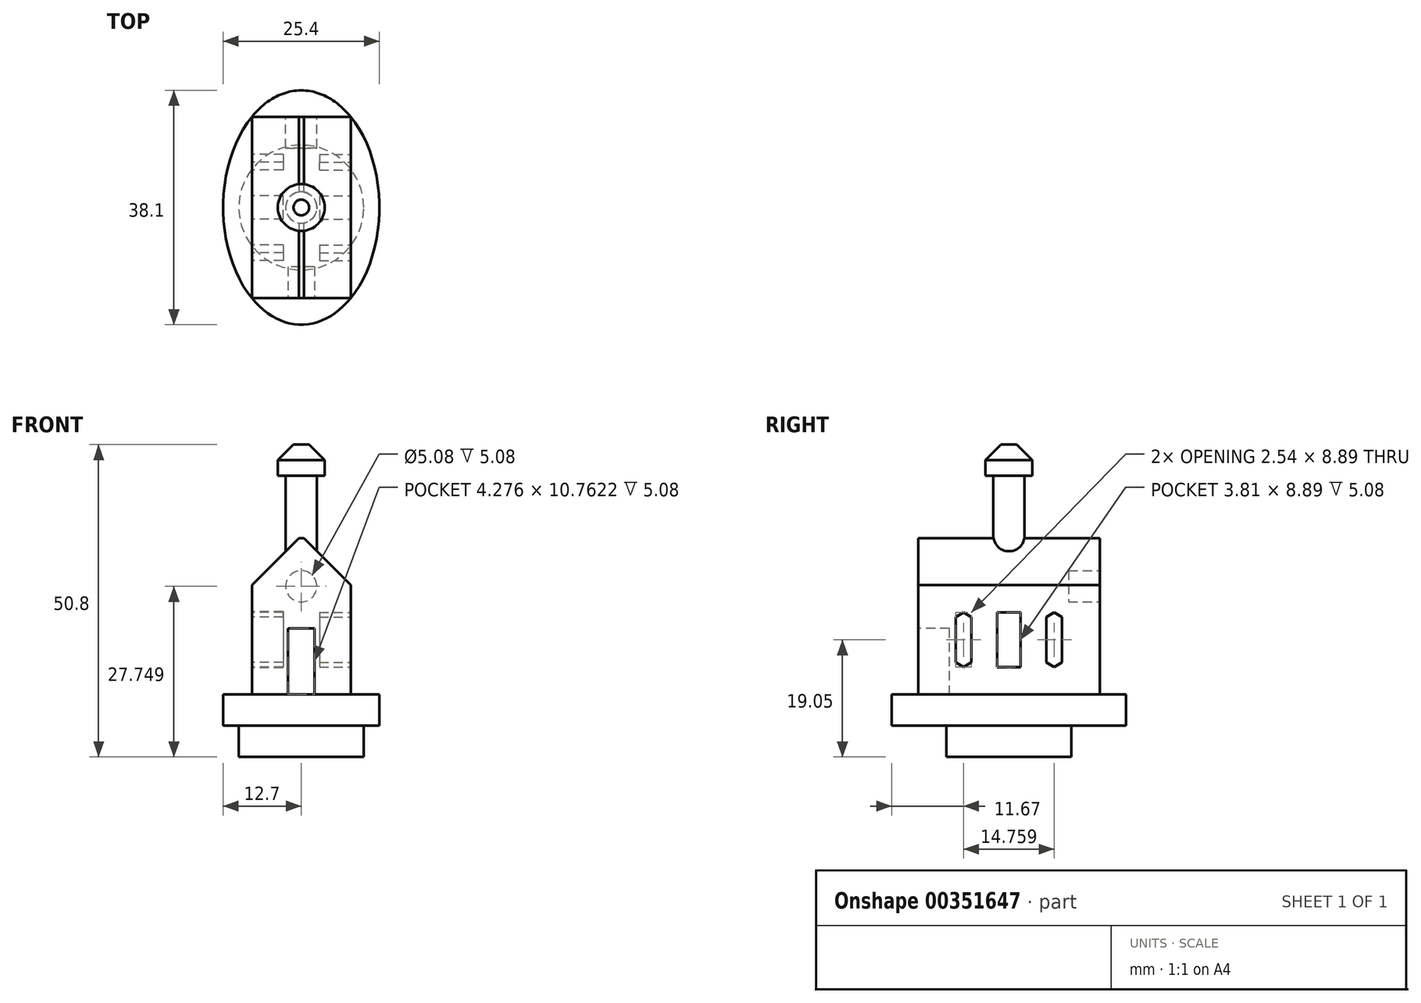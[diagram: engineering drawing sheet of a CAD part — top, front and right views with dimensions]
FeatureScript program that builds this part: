
annotation { "Feature Type Name" : "Feature", "Feature Type Description" : "" }
export const myFeature = defineFeature(function(context is Context, id is Id, definition is map)
    precondition{}
    {
        {
            var Q0;
            Q0=qCreatedBy(makeId("Top.planeOp"),FACE);
            var sketch = newSketch(context, id + "F0", { "sketchPlane" : qUnion([Q0])});
            skCircle(sketch, "E0", {"center": v(0, 0) * mm, "radius": 10.16 * mm});
            skSolve(sketch);
        }
        {
            var Q0;
            Q0 = qSketchRegion(id + "F0", true);
            extrude(context, id + "F1", {"entities" : qUnion([Q0]), "depth" : 5.08 * mm});
        }
        {
            var Q0;
            Q0=makeQuery(id+"F1.opExtrude","CAP_FACE",FACE,{"disambiguationData":[OSD([sQuery(id+"F0.wireOp",EDGE,"E0")])],"isStart":false});
            var sketch = newSketch(context, id + "F2", { "sketchPlane" : qUnion([Q0])});
            skEllipse(sketch, "E1", {"center": v(0, 0) * mm, "majorRadius": 19.05 * mm, "minorRadius": 12.7 * mm, "majorAxis": v(0, 1)});
            skSolve(sketch);
        }
        {
            var Q0;
            Q0 = qSketchRegion(id + "F2", true);
            extrude(context, id + "F3", {"entities" : qUnion([Q0]), "operationType" : NewBodyOperationType.ADD, "depth" : 5.08 * mm});
        }
        {
            var Q0;
            Q0=makeQuery(id+"F3.opExtrude","CAP_FACE",FACE,{"disambiguationData":[OSD([sQuery(id+"F2.wireOp",EDGE,"E1")])],"isStart":false});
            var sketch = newSketch(context, id + "F4", { "sketchPlane" : qUnion([Q0])});
            skLineSegment(sketch, "E2.bottom", {"start": v(8.03, 14.76) * mm, "end": v(-8.03, 14.76) * mm});
            skLineSegment(sketch, "E2.top", {"start": v(8.03, -14.76) * mm, "end": v(-8.03, -14.76) * mm});
            skLineSegment(sketch, "E2.left", {"start": v(8.03, 14.76) * mm, "end": v(8.03, -14.76) * mm});
            skLineSegment(sketch, "E2.right", {"start": v(-8.03, 14.76) * mm, "end": v(-8.03, -14.76) * mm});
            skPoint(sketch, "E2.middle", {"position": v(0, 0) * mm});
            skSolve(sketch);
        }
        {
            var Q0;
            Q0 = qSketchRegion(id + "F4", true);
            extrude(context, id + "F5", {"entities" : qUnion([Q0]), "operationType" : NewBodyOperationType.ADD, "depth" : 25.4 * mm});
        }
        {
            var Q0;
            Q0=makeQuery(id+"F5.opExtrude","CAP_FACE",FACE,{"disambiguationData":[OSD([sQuery(id+"F4.wireOp",EDGE,"E2.bottom"),sQuery(id+"F4.wireOp",EDGE,"E2.top"),sQuery(id+"F4.wireOp",EDGE,"E2.left"),sQuery(id+"F4.wireOp",EDGE,"E2.right")])],"isStart":false});
            var sketch = newSketch(context, id + "F6", { "sketchPlane" : qUnion([Q0])});
            skCircle(sketch, "E3", {"center": v(0, 0) * mm, "radius": 2.54 * mm});
            skSolve(sketch);
        }
        {
            var Q0;
            Q0=makeQuery(id+"F6.imprint","IMPRINT",FACE,{"disambiguationData":[TD([[makeQuery(id+"F6.imprint","IMPRINT",EDGE,{"derivedFrom":sQuery(id+"F6.wireOp",EDGE,"E3")}),1.0]])]});
            extrude(context, id + "F7", {"entities" : qUnion([Q0]), "operationType" : NewBodyOperationType.ADD, "depth" : 10.16 * mm});
        }
        {
            var Q0;
            Q0=makeQuery(id+"F7.opExtrude","CAP_FACE",FACE,{"disambiguationData":[OSD([sQuery(id+"F6.wireOp",EDGE,"E3")])],"isStart":false});
            var sketch = newSketch(context, id + "F8", { "sketchPlane" : qUnion([Q0])});
            skCircle(sketch, "E4", {"center": v(0, 0) * mm, "radius": 3.81 * mm});
            skSolve(sketch);
        }
        {
            var Q0;
            Q0 = qSketchRegion(id + "F8", true);
            extrude(context, id + "F9", {"entities" : qUnion([Q0]), "operationType" : NewBodyOperationType.ADD, "depth" : 5.08 * mm});
        }
        {
            var Q0;
            Q0=makeQuery(id+"F9.opExtrude","CAP_EDGE",EDGE,{"disambiguationData":[OSD([sQuery(id+"F8.wireOp",EDGE,"E4")])],"isStart":false});
            chamfer(context, id + "F10", {"entities" : qUnion([Q0]), "width" : 2.54 * mm, "tangentPropagation" : true});
        }
        {
            var Q0;
            Q0=makeQuery(id+"F5.opExtrude","CAP_EDGE",EDGE,{"disambiguationData":[OSD([sQuery(id+"F4.wireOp",EDGE,"E2.right")])],"isStart":false});
            var Q1;
            Q1=makeQuery(id+"F5.opExtrude","CAP_EDGE",EDGE,{"disambiguationData":[OSD([sQuery(id+"F4.wireOp",EDGE,"E2.left")])],"isStart":false});
            chamfer(context, id + "F11", {"entities" : qUnion([Q0, Q1]), "width" : 7.62 * mm, "tangentPropagation" : true});
        }
        {
            var Q0;
            Q0=makeQuery(id+"F5.opExtrude","SWEPT_FACE",FACE,{"disambiguationData":[OSD([sQuery(id+"F4.wireOp",EDGE,"E2.top")])]});
            var sketch = newSketch(context, id + "F12", { "sketchPlane" : qUnion([Q0])});
            skPoint(sketch, "E5", {"position": v(0, 15.54) * mm});
            skLineSegment(sketch, "E6.bottom", {"start": v(2.14, 10.16) * mm, "end": v(-2.14, 10.16) * mm});
            skLineSegment(sketch, "E6.top", {"start": v(2.14, 20.92) * mm, "end": v(-2.14, 20.92) * mm});
            skLineSegment(sketch, "E6.left", {"start": v(2.14, 10.16) * mm, "end": v(2.14, 20.92) * mm});
            skLineSegment(sketch, "E6.right", {"start": v(-2.14, 10.16) * mm, "end": v(-2.14, 20.92) * mm});
            skSolve(sketch);
        }
        {
            var Q0;
            Q0 = qSketchRegion(id + "F12", true);
            extrude(context, id + "F13", {"entities" : qUnion([Q0]), "operationType" : NewBodyOperationType.REMOVE, "oppositeDirection" : true, "depth" : 5.08 * mm});
        }
        {
            var Q0;
            Q0=makeQuery(id+"F5.opExtrude","SWEPT_FACE",FACE,{"disambiguationData":[OSD([sQuery(id+"F4.wireOp",EDGE,"E2.bottom")])]});
            var sketch = newSketch(context, id + "F14", { "sketchPlane" : qUnion([Q0])});
            skPoint(sketch, "E7", {"position": v(0, 36.48) * mm});
            skCircle(sketch, "E8", {"center": v(0, 36.48) * mm, "radius": 2.54 * mm});
            skPoint(sketch, "E9", {"position": v(0, 19.4) * mm});
            skCircle(sketch, "E10", {"center": v(0, 19.4) * mm, "radius": 2.54 * mm});
            skPoint(sketch, "E11", {"position": v(0, 27.75) * mm});
            skCircle(sketch, "E12", {"center": v(0, 27.75) * mm, "radius": 2.54 * mm});
            skPoint(sketch, "E13", {"position": v(0, 31.87) * mm});
            skCircle(sketch, "E14", {"center": v(0, 31.87) * mm, "radius": 2.54 * mm});
            skSolve(sketch);
        }
        {
            var Q0;
            {var subQ0=sQuery(id+"F14.wireOp",EDGE,"E14");var subQ1=sQuery(id+"F14.wireOp",EDGE,"E12");var subQ2=makeQuery(id+"F14.imprint","INTERSECT",VERTEX,{"disambiguationData":[OD(0.0)],"derivedFrom":[subQ1,subQ0]});Q0=makeQuery(id+"F14.imprint","IMPRINT",FACE,{"disambiguationData":[TD([[makeQuery(id+"F14.imprint","IMPRINT",EDGE,{"disambiguationData":[TD([[subQ2,1.0]])],"derivedFrom":subQ1}),1.0]])]});}
            var Q1;
            {var subQ0=sQuery(id+"F14.wireOp",EDGE,"E14");var subQ1=sQuery(id+"F14.wireOp",EDGE,"E12");var subQ2=makeQuery(id+"F14.imprint","INTERSECT",VERTEX,{"disambiguationData":[OD(0.0)],"derivedFrom":[subQ1,subQ0]});Q1=makeQuery(id+"F14.imprint","IMPRINT",FACE,{"disambiguationData":[TD([[makeQuery(id+"F14.imprint","IMPRINT",EDGE,{"disambiguationData":[TD([[subQ2,-1.0]])],"derivedFrom":subQ1}),1.0]])]});}
            extrude(context, id + "F15", {"entities" : qUnion([Q0, Q1]), "operationType" : NewBodyOperationType.REMOVE, "oppositeDirection" : true, "depth" : 5.08 * mm});
        }
        {
            var Q0;
            Q0=makeQuery(id+"F5.opExtrude","SWEPT_FACE",FACE,{"disambiguationData":[OSD([sQuery(id+"F4.wireOp",EDGE,"E2.left")])]});
            var sketch = newSketch(context, id + "F16", { "sketchPlane" : qUnion([Q0])});
            skLineSegment(sketch, "E15", {"start": v(14.76, 27.94) * mm, "end": v(-14.76, 10.16) * mm});
            skLineSegment(sketch, "E16", {"start": v(-14.76, 10.16) * mm, "end": v(-14.76, 27.94) * mm});
            skLineSegment(sketch, "E17", {"start": v(-14.76, 27.94) * mm, "end": v(14.76, 10.16) * mm});
            skLineSegment(sketch, "E18", {"start": v(14.76, 10.16) * mm, "end": v(14.76, 27.94) * mm});
            skLineSegment(sketch, "E19", {"start": v(0, 27.94) * mm, "end": v(0, 10.16) * mm});
            skLineSegment(sketch, "E20", {"start": v(0, 10.16) * mm, "end": v(-14.76, 19.05) * mm});
            skLineSegment(sketch, "E21", {"start": v(-14.76, 19.05) * mm, "end": v(0, 27.94) * mm});
            skLineSegment(sketch, "E22", {"start": v(0, 27.94) * mm, "end": v(14.76, 19.05) * mm});
            skLineSegment(sketch, "E23", {"start": v(14.76, 19.05) * mm, "end": v(0, 10.16) * mm});
            skLineSegment(sketch, "E24.bottom", {"start": v(1.9, 23.5) * mm, "end": v(-1.9, 23.5) * mm});
            skLineSegment(sketch, "E24.top", {"start": v(1.9, 14.6) * mm, "end": v(-1.9, 14.6) * mm});
            skLineSegment(sketch, "E24.left", {"start": v(1.9, 23.5) * mm, "end": v(1.9, 14.6) * mm});
            skLineSegment(sketch, "E24.right", {"start": v(-1.9, 23.5) * mm, "end": v(-1.9, 14.6) * mm});
            skPoint(sketch, "E24.middle", {"position": v(0, 19.05) * mm});
            skPoint(sketch, "E24.cornerSnap0", {"position": v(7.38, 23.5) * mm});
            skLineSegment(sketch, "E25", {"start": v(-14.76, 19.05) * mm, "end": v(14.76, 19.05) * mm});
            skLineSegment(sketch, "E26", {"start": v(7.38, 23.5) * mm, "end": v(7.38, 14.6) * mm});
            skLineSegment(sketch, "E27", {"start": v(7.38, 14.6) * mm, "end": v(-7.38, 23.5) * mm});
            skLineSegment(sketch, "E28", {"start": v(-7.38, 23.5) * mm, "end": v(-7.38, 14.6) * mm});
            skLineSegment(sketch, "E29.bottom", {"start": v(-6.1, 23.52) * mm, "end": v(-8.65, 23.52) * mm});
            skLineSegment(sketch, "E29.top", {"start": v(-6.1, 14.58) * mm, "end": v(-8.65, 14.58) * mm});
            skLineSegment(sketch, "E29.left", {"start": v(-6.1, 23.52) * mm, "end": v(-6.1, 14.58) * mm});
            skLineSegment(sketch, "E29.right", {"start": v(-8.65, 23.52) * mm, "end": v(-8.65, 14.58) * mm});
            skPoint(sketch, "E29.middle", {"position": v(-7.38, 19.05) * mm});
            skLineSegment(sketch, "E30.bottom", {"start": v(8.65, 23.62) * mm, "end": v(6.1, 23.62) * mm});
            skLineSegment(sketch, "E30.top", {"start": v(8.65, 14.48) * mm, "end": v(6.1, 14.48) * mm});
            skLineSegment(sketch, "E30.left", {"start": v(8.65, 23.62) * mm, "end": v(8.65, 14.48) * mm});
            skLineSegment(sketch, "E30.right", {"start": v(6.1, 23.62) * mm, "end": v(6.1, 14.48) * mm});
            skPoint(sketch, "E30.middle", {"position": v(7.38, 19.05) * mm});
            skSolve(sketch);
        }
        {
            var Q0;
            {var subQ3=sQuery(id+"F16.wireOp",EDGE,"E29.right");var subQ5=sQuery(id+"F16.wireOp",EDGE,"E25");var subQ6=makeQuery(id+"F16.imprint","INTERSECT",VERTEX,{"derivedFrom":[subQ5,subQ3]});Q0=makeQuery(id+"F16.imprint","IMPRINT",FACE,{"disambiguationData":[TD([[makeQuery(id+"F16.imprint","IMPRINT",EDGE,{"disambiguationData":[TD([[subQ6,-1.0]])],"derivedFrom":subQ5}),1.0]])]});}
            var Q1;
            {var subQ0=sQuery(id+"F16.wireOp",EDGE,"E28");var subQ1=sQuery(id+"F16.wireOp",EDGE,"E25");var subQ2=makeQuery(id+"F16.imprint","INTERSECT",VERTEX,{"derivedFrom":[subQ1,subQ0]});Q1=makeQuery(id+"F16.imprint","IMPRINT",FACE,{"disambiguationData":[TD([[makeQuery(id+"F16.imprint","IMPRINT",EDGE,{"disambiguationData":[TD([[subQ2,-1.0]])],"derivedFrom":subQ1}),1.0]])]});}
            var Q2;
            {var subQ0=sQuery(id+"F16.wireOp",EDGE,"E28");var subQ5=sQuery(id+"F16.wireOp",EDGE,"E25");var subQ6=makeQuery(id+"F16.imprint","INTERSECT",VERTEX,{"derivedFrom":[subQ5,subQ0]});Q2=makeQuery(id+"F16.imprint","IMPRINT",FACE,{"disambiguationData":[TD([[makeQuery(id+"F16.imprint","IMPRINT",EDGE,{"disambiguationData":[TD([[subQ6,-1.0]])],"derivedFrom":subQ5}),-1.0]])]});}
            var Q3;
            {var subQ3=sQuery(id+"F16.wireOp",EDGE,"E29.right");var subQ5=sQuery(id+"F16.wireOp",EDGE,"E25");var subQ7=makeQuery(id+"F16.imprint","INTERSECT",VERTEX,{"derivedFrom":[subQ5,subQ3]});Q3=makeQuery(id+"F16.imprint","IMPRINT",FACE,{"disambiguationData":[TD([[makeQuery(id+"F16.imprint","IMPRINT",EDGE,{"disambiguationData":[TD([[subQ7,-1.0]])],"derivedFrom":subQ5}),-1.0]])]});}
            var Q4;
            {var subQ0=sQuery(id+"F16.wireOp",EDGE,"E24.bottom");var subQ5=sQuery(id+"F16.wireOp",EDGE,"E24.right");var subQ6=makeQuery(id+"F16.imprint","INTERSECT",VERTEX,{"derivedFrom":[subQ0,subQ5]});Q4=makeQuery(id+"F16.imprint","IMPRINT",FACE,{"disambiguationData":[TD([[makeQuery(id+"F16.imprint","IMPRINT",EDGE,{"disambiguationData":[TD([[subQ6,1.0]])],"derivedFrom":subQ0}),1.0]])]});}
            var Q5;
            {var subQ0=sQuery(id+"F16.wireOp",EDGE,"E24.left");var subQ5=sQuery(id+"F16.wireOp",EDGE,"E24.bottom");var subQ7=makeQuery(id+"F16.imprint","INTERSECT",VERTEX,{"derivedFrom":[subQ5,subQ0]});Q5=makeQuery(id+"F16.imprint","IMPRINT",FACE,{"disambiguationData":[TD([[makeQuery(id+"F16.imprint","IMPRINT",EDGE,{"disambiguationData":[TD([[subQ7,-1.0]])],"derivedFrom":subQ5}),1.0]])]});}
            var Q6;
            {var subQ0=sQuery(id+"F16.wireOp",EDGE,"E27");var subQ1=sQuery(id+"F16.wireOp",EDGE,"E24.right");var subQ2=makeQuery(id+"F16.imprint","INTERSECT",VERTEX,{"derivedFrom":[subQ1,subQ0]});Q6=makeQuery(id+"F16.imprint","IMPRINT",FACE,{"disambiguationData":[TD([[makeQuery(id+"F16.imprint","IMPRINT",EDGE,{"disambiguationData":[TD([[subQ2,-1.0]])],"derivedFrom":subQ1}),1.0]])]});}
            var Q7;
            {var subQ0=sQuery(id+"F16.wireOp",EDGE,"E24.left");var subQ1=sQuery(id+"F16.wireOp",EDGE,"E15");var subQ2=makeQuery(id+"F16.imprint","INTERSECT",VERTEX,{"derivedFrom":[subQ1,subQ0]});Q7=makeQuery(id+"F16.imprint","IMPRINT",FACE,{"disambiguationData":[TD([[makeQuery(id+"F16.imprint","IMPRINT",EDGE,{"disambiguationData":[TD([[subQ2,-1.0]])],"derivedFrom":subQ0}),-1.0]])]});}
            var Q8;
            {var subQ0=sQuery(id+"F16.wireOp",EDGE,"E25");var subQ1=sQuery(id+"F16.wireOp",EDGE,"E24.left");var subQ2=makeQuery(id+"F16.imprint","INTERSECT",VERTEX,{"derivedFrom":[subQ1,subQ0]});Q8=makeQuery(id+"F16.imprint","IMPRINT",FACE,{"disambiguationData":[TD([[makeQuery(id+"F16.imprint","IMPRINT",EDGE,{"disambiguationData":[TD([[subQ2,-1.0]])],"derivedFrom":subQ1}),-1.0]])]});}
            var Q9;
            {var subQ0=sQuery(id+"F16.wireOp",EDGE,"E24.top");var subQ5=sQuery(id+"F16.wireOp",EDGE,"E24.left");var subQ6=makeQuery(id+"F16.imprint","INTERSECT",VERTEX,{"derivedFrom":[subQ0,subQ5]});Q9=makeQuery(id+"F16.imprint","IMPRINT",FACE,{"disambiguationData":[TD([[makeQuery(id+"F16.imprint","IMPRINT",EDGE,{"disambiguationData":[TD([[subQ6,-1.0]])],"derivedFrom":subQ0}),-1.0]])]});}
            var Q10;
            {var subQ0=sQuery(id+"F16.wireOp",EDGE,"E24.right");var subQ5=sQuery(id+"F16.wireOp",EDGE,"E24.top");var subQ7=makeQuery(id+"F16.imprint","INTERSECT",VERTEX,{"derivedFrom":[subQ5,subQ0]});Q10=makeQuery(id+"F16.imprint","IMPRINT",FACE,{"disambiguationData":[TD([[makeQuery(id+"F16.imprint","IMPRINT",EDGE,{"disambiguationData":[TD([[subQ7,1.0]])],"derivedFrom":subQ5}),-1.0]])]});}
            var Q11;
            {var subQ0=sQuery(id+"F16.wireOp",EDGE,"E24.right");var subQ1=sQuery(id+"F16.wireOp",EDGE,"E15");var subQ2=makeQuery(id+"F16.imprint","INTERSECT",VERTEX,{"derivedFrom":[subQ1,subQ0]});Q11=makeQuery(id+"F16.imprint","IMPRINT",FACE,{"disambiguationData":[TD([[makeQuery(id+"F16.imprint","IMPRINT",EDGE,{"disambiguationData":[TD([[subQ2,1.0]])],"derivedFrom":subQ0}),1.0]])]});}
            var Q12;
            {var subQ0=sQuery(id+"F16.wireOp",EDGE,"E30.right");var subQ1=sQuery(id+"F16.wireOp",EDGE,"E25");var subQ2=makeQuery(id+"F16.imprint","INTERSECT",VERTEX,{"derivedFrom":[subQ1,subQ0]});Q12=makeQuery(id+"F16.imprint","IMPRINT",FACE,{"disambiguationData":[TD([[makeQuery(id+"F16.imprint","IMPRINT",EDGE,{"disambiguationData":[TD([[subQ2,-1.0]])],"derivedFrom":subQ1}),-1.0]])]});}
            var Q13;
            {var subQ0=sQuery(id+"F16.wireOp",EDGE,"E26");var subQ5=sQuery(id+"F16.wireOp",EDGE,"E25");var subQ6=makeQuery(id+"F16.imprint","INTERSECT",VERTEX,{"derivedFrom":[subQ5,subQ0]});Q13=makeQuery(id+"F16.imprint","IMPRINT",FACE,{"disambiguationData":[TD([[makeQuery(id+"F16.imprint","IMPRINT",EDGE,{"disambiguationData":[TD([[subQ6,-1.0]])],"derivedFrom":subQ5}),-1.0]])]});}
            var Q14;
            {var subQ0=sQuery(id+"F16.wireOp",EDGE,"E26");var subQ5=sQuery(id+"F16.wireOp",EDGE,"E25");var subQ6=makeQuery(id+"F16.imprint","INTERSECT",VERTEX,{"derivedFrom":[subQ5,subQ0]});Q14=makeQuery(id+"F16.imprint","IMPRINT",FACE,{"disambiguationData":[TD([[makeQuery(id+"F16.imprint","IMPRINT",EDGE,{"disambiguationData":[TD([[subQ6,-1.0]])],"derivedFrom":subQ5}),1.0]])]});}
            var Q15;
            {var subQ3=sQuery(id+"F16.wireOp",EDGE,"E30.right");var subQ5=sQuery(id+"F16.wireOp",EDGE,"E25");var subQ6=makeQuery(id+"F16.imprint","INTERSECT",VERTEX,{"derivedFrom":[subQ5,subQ3]});Q15=makeQuery(id+"F16.imprint","IMPRINT",FACE,{"disambiguationData":[TD([[makeQuery(id+"F16.imprint","IMPRINT",EDGE,{"disambiguationData":[TD([[subQ6,-1.0]])],"derivedFrom":subQ5}),1.0]])]});}
            extrude(context, id + "F17", {"entities" : qUnion([Q0, Q1, Q2, Q3, Q4, Q5, Q6, Q7, Q8, Q9, Q10, Q11, Q12, Q13, Q14, Q15]), "operationType" : NewBodyOperationType.REMOVE, "oppositeDirection" : true, "depth" : 5.08 * mm});
        }
        {
            var Q0;
            Q0=makeQuery(id+"F5.opExtrude","SWEPT_FACE",FACE,{"disambiguationData":[OSD([sQuery(id+"F4.wireOp",EDGE,"E2.right")])]});
            var sketch = newSketch(context, id + "F18", { "sketchPlane" : qUnion([Q0])});
            skLineSegment(sketch, "E31", {"start": v(-14.76, 27.94) * mm, "end": v(14.76, 10.16) * mm});
            skLineSegment(sketch, "E32", {"start": v(14.76, 10.16) * mm, "end": v(14.76, 27.94) * mm});
            skLineSegment(sketch, "E33", {"start": v(14.76, 27.94) * mm, "end": v(-14.76, 10.16) * mm});
            skLineSegment(sketch, "E34", {"start": v(-14.76, 10.16) * mm, "end": v(-14.76, 27.94) * mm});
            skLineSegment(sketch, "E35", {"start": v(0, 27.94) * mm, "end": v(0, 10.16) * mm});
            skLineSegment(sketch, "E36", {"start": v(0, 10.16) * mm, "end": v(-14.76, 19.05) * mm});
            skLineSegment(sketch, "E37", {"start": v(-14.76, 19.05) * mm, "end": v(0, 27.94) * mm});
            skLineSegment(sketch, "E38", {"start": v(14.76, 19.05) * mm, "end": v(0, 27.94) * mm});
            skLineSegment(sketch, "E39", {"start": v(0, 10.16) * mm, "end": v(14.76, 19.05) * mm});
            skLineSegment(sketch, "E40", {"start": v(-14.76, 19.05) * mm, "end": v(14.76, 19.05) * mm});
            skLineSegment(sketch, "E41", {"start": v(-7.38, 23.5) * mm, "end": v(-7.38, 14.6) * mm});
            skLineSegment(sketch, "E42", {"start": v(-7.38, 14.6) * mm, "end": v(7.38, 23.5) * mm});
            skLineSegment(sketch, "E43", {"start": v(7.38, 23.5) * mm, "end": v(7.38, 14.6) * mm});
            skLineSegment(sketch, "E44.bottom", {"start": v(1.9, 23.62) * mm, "end": v(-1.9, 23.62) * mm});
            skLineSegment(sketch, "E44.top", {"start": v(1.9, 14.48) * mm, "end": v(-1.9, 14.48) * mm});
            skLineSegment(sketch, "E44.left", {"start": v(1.9, 23.62) * mm, "end": v(1.9, 14.48) * mm});
            skLineSegment(sketch, "E44.right", {"start": v(-1.9, 23.62) * mm, "end": v(-1.9, 14.48) * mm});
            skPoint(sketch, "E44.middle", {"position": v(0, 19.05) * mm});
            skLineSegment(sketch, "E45.bottom", {"start": v(8.65, 23.62) * mm, "end": v(6.1, 23.62) * mm});
            skLineSegment(sketch, "E45.top", {"start": v(8.65, 14.48) * mm, "end": v(6.1, 14.48) * mm});
            skLineSegment(sketch, "E45.left", {"start": v(8.65, 23.62) * mm, "end": v(8.65, 14.48) * mm});
            skLineSegment(sketch, "E45.right", {"start": v(6.1, 23.62) * mm, "end": v(6.1, 14.48) * mm});
            skPoint(sketch, "E45.middle", {"position": v(7.38, 19.05) * mm});
            skLineSegment(sketch, "E46.bottom", {"start": v(-6.1, 23.62) * mm, "end": v(-8.65, 23.62) * mm});
            skLineSegment(sketch, "E46.top", {"start": v(-6.1, 14.48) * mm, "end": v(-8.65, 14.48) * mm});
            skLineSegment(sketch, "E46.left", {"start": v(-6.1, 23.62) * mm, "end": v(-6.1, 14.48) * mm});
            skLineSegment(sketch, "E46.right", {"start": v(-8.65, 23.62) * mm, "end": v(-8.65, 14.48) * mm});
            skPoint(sketch, "E46.middle", {"position": v(-7.38, 19.05) * mm});
            skSolve(sketch);
        }
        {
            var Q0;
            {var subQ1=sQuery(id+"F18.wireOp",EDGE,"E41");var subQ7=sQuery(id+"F18.wireOp",EDGE,"E40");var subQ8=makeQuery(id+"F18.imprint","INTERSECT",VERTEX,{"derivedFrom":[subQ7,subQ1]});Q0=makeQuery(id+"F18.imprint","IMPRINT",FACE,{"disambiguationData":[TD([[makeQuery(id+"F18.imprint","IMPRINT",EDGE,{"disambiguationData":[TD([[subQ8,-1.0]])],"derivedFrom":subQ7}),-1.0]])]});}
            var Q1;
            {var subQ1=sQuery(id+"F18.wireOp",EDGE,"E37");var subQ5=sQuery(id+"F18.wireOp",EDGE,"E46.right");var subQ9=makeQuery(id+"F18.imprint","INTERSECT",VERTEX,{"derivedFrom":[subQ1,subQ5]});Q1=makeQuery(id+"F18.imprint","IMPRINT",FACE,{"disambiguationData":[TD([[makeQuery(id+"F18.imprint","IMPRINT",EDGE,{"disambiguationData":[TD([[subQ9,-1.0]])],"derivedFrom":subQ1}),-1.0]])]});}
            var Q2;
            {var subQ0=sQuery(id+"F18.wireOp",EDGE,"E44.right");var subQ5=sQuery(id+"F18.wireOp",EDGE,"E44.bottom");var subQ7=makeQuery(id+"F18.imprint","INTERSECT",VERTEX,{"derivedFrom":[subQ5,subQ0]});Q2=makeQuery(id+"F18.imprint","IMPRINT",FACE,{"disambiguationData":[TD([[makeQuery(id+"F18.imprint","IMPRINT",EDGE,{"disambiguationData":[TD([[subQ7,1.0]])],"derivedFrom":subQ5}),1.0]])]});}
            var Q3;
            {var subQ0=sQuery(id+"F18.wireOp",EDGE,"E44.right");var subQ1=sQuery(id+"F18.wireOp",EDGE,"E31");var subQ2=makeQuery(id+"F18.imprint","INTERSECT",VERTEX,{"derivedFrom":[subQ1,subQ0]});Q3=makeQuery(id+"F18.imprint","IMPRINT",FACE,{"disambiguationData":[TD([[makeQuery(id+"F18.imprint","IMPRINT",EDGE,{"disambiguationData":[TD([[subQ2,-1.0]])],"derivedFrom":subQ0}),1.0]])]});}
            var Q4;
            {var subQ0=sQuery(id+"F18.wireOp",EDGE,"E44.right");var subQ1=sQuery(id+"F18.wireOp",EDGE,"E40");var subQ2=makeQuery(id+"F18.imprint","INTERSECT",VERTEX,{"derivedFrom":[subQ1,subQ0]});Q4=makeQuery(id+"F18.imprint","IMPRINT",FACE,{"disambiguationData":[TD([[makeQuery(id+"F18.imprint","IMPRINT",EDGE,{"disambiguationData":[TD([[subQ2,-1.0]])],"derivedFrom":subQ0}),1.0]])]});}
            var Q5;
            {var subQ0=sQuery(id+"F18.wireOp",EDGE,"E44.top");var subQ5=sQuery(id+"F18.wireOp",EDGE,"E44.right");var subQ7=makeQuery(id+"F18.imprint","INTERSECT",VERTEX,{"derivedFrom":[subQ0,subQ5]});Q5=makeQuery(id+"F18.imprint","IMPRINT",FACE,{"disambiguationData":[TD([[makeQuery(id+"F18.imprint","IMPRINT",EDGE,{"disambiguationData":[TD([[subQ7,1.0]])],"derivedFrom":subQ0}),-1.0]])]});}
            var Q6;
            {var subQ0=sQuery(id+"F18.wireOp",EDGE,"E44.left");var subQ5=sQuery(id+"F18.wireOp",EDGE,"E44.top");var subQ7=makeQuery(id+"F18.imprint","INTERSECT",VERTEX,{"derivedFrom":[subQ5,subQ0]});Q6=makeQuery(id+"F18.imprint","IMPRINT",FACE,{"disambiguationData":[TD([[makeQuery(id+"F18.imprint","IMPRINT",EDGE,{"disambiguationData":[TD([[subQ7,-1.0]])],"derivedFrom":subQ5}),-1.0]])]});}
            var Q7;
            {var subQ0=sQuery(id+"F18.wireOp",EDGE,"E44.left");var subQ1=sQuery(id+"F18.wireOp",EDGE,"E31");var subQ2=makeQuery(id+"F18.imprint","INTERSECT",VERTEX,{"derivedFrom":[subQ1,subQ0]});Q7=makeQuery(id+"F18.imprint","IMPRINT",FACE,{"disambiguationData":[TD([[makeQuery(id+"F18.imprint","IMPRINT",EDGE,{"disambiguationData":[TD([[subQ2,1.0]])],"derivedFrom":subQ0}),-1.0]])]});}
            var Q8;
            {var subQ0=sQuery(id+"F18.wireOp",EDGE,"E44.left");var subQ1=sQuery(id+"F18.wireOp",EDGE,"E40");var subQ2=makeQuery(id+"F18.imprint","INTERSECT",VERTEX,{"derivedFrom":[subQ1,subQ0]});Q8=makeQuery(id+"F18.imprint","IMPRINT",FACE,{"disambiguationData":[TD([[makeQuery(id+"F18.imprint","IMPRINT",EDGE,{"disambiguationData":[TD([[subQ2,1.0]])],"derivedFrom":subQ0}),-1.0]])]});}
            var Q9;
            {var subQ0=sQuery(id+"F18.wireOp",EDGE,"E44.bottom");var subQ5=sQuery(id+"F18.wireOp",EDGE,"E44.left");var subQ6=makeQuery(id+"F18.imprint","INTERSECT",VERTEX,{"derivedFrom":[subQ0,subQ5]});Q9=makeQuery(id+"F18.imprint","IMPRINT",FACE,{"disambiguationData":[TD([[makeQuery(id+"F18.imprint","IMPRINT",EDGE,{"disambiguationData":[TD([[subQ6,-1.0]])],"derivedFrom":subQ0}),1.0]])]});}
            var Q10;
            {var subQ1=sQuery(id+"F18.wireOp",EDGE,"E40");var subQ7=sQuery(id+"F18.wireOp",EDGE,"E45.right");var subQ8=makeQuery(id+"F18.imprint","INTERSECT",VERTEX,{"derivedFrom":[subQ1,subQ7]});Q10=makeQuery(id+"F18.imprint","IMPRINT",FACE,{"disambiguationData":[TD([[makeQuery(id+"F18.imprint","IMPRINT",EDGE,{"disambiguationData":[TD([[subQ8,-1.0]])],"derivedFrom":subQ1}),1.0]])]});}
            var Q11;
            {var subQ1=sQuery(id+"F18.wireOp",EDGE,"E38");var subQ7=sQuery(id+"F18.wireOp",EDGE,"E45.left");var subQ9=makeQuery(id+"F18.imprint","INTERSECT",VERTEX,{"derivedFrom":[subQ1,subQ7]});Q11=makeQuery(id+"F18.imprint","IMPRINT",FACE,{"disambiguationData":[TD([[makeQuery(id+"F18.imprint","IMPRINT",EDGE,{"disambiguationData":[TD([[subQ9,-1.0]])],"derivedFrom":subQ1}),1.0]])]});}
            var Q12;
            {var subQ1=sQuery(id+"F18.wireOp",EDGE,"E31");var subQ7=sQuery(id+"F18.wireOp",EDGE,"E45.right");var subQ9=makeQuery(id+"F18.imprint","INTERSECT",VERTEX,{"derivedFrom":[subQ1,subQ7]});Q12=makeQuery(id+"F18.imprint","IMPRINT",FACE,{"disambiguationData":[TD([[makeQuery(id+"F18.imprint","IMPRINT",EDGE,{"disambiguationData":[TD([[subQ9,-1.0]])],"derivedFrom":subQ1}),1.0]])]});}
            var Q13;
            {var subQ0=sQuery(id+"F18.wireOp",EDGE,"E41");var subQ5=sQuery(id+"F18.wireOp",EDGE,"E40");var subQ6=makeQuery(id+"F18.imprint","INTERSECT",VERTEX,{"derivedFrom":[subQ5,subQ0]});Q13=makeQuery(id+"F18.imprint","IMPRINT",FACE,{"disambiguationData":[TD([[makeQuery(id+"F18.imprint","IMPRINT",EDGE,{"disambiguationData":[TD([[subQ6,-1.0]])],"derivedFrom":subQ5}),1.0]])]});}
            var Q14;
            {var subQ3=sQuery(id+"F18.wireOp",EDGE,"E46.right");var subQ5=sQuery(id+"F18.wireOp",EDGE,"E40");var subQ6=makeQuery(id+"F18.imprint","INTERSECT",VERTEX,{"derivedFrom":[subQ5,subQ3]});Q14=makeQuery(id+"F18.imprint","IMPRINT",FACE,{"disambiguationData":[TD([[makeQuery(id+"F18.imprint","IMPRINT",EDGE,{"disambiguationData":[TD([[subQ6,-1.0]])],"derivedFrom":subQ5}),-1.0]])]});}
            var Q15;
            {var subQ0=sQuery(id+"F18.wireOp",EDGE,"E43");var subQ5=sQuery(id+"F18.wireOp",EDGE,"E40");var subQ6=makeQuery(id+"F18.imprint","INTERSECT",VERTEX,{"derivedFrom":[subQ5,subQ0]});Q15=makeQuery(id+"F18.imprint","IMPRINT",FACE,{"disambiguationData":[TD([[makeQuery(id+"F18.imprint","IMPRINT",EDGE,{"disambiguationData":[TD([[subQ6,-1.0]])],"derivedFrom":subQ5}),-1.0]])]});}
            extrude(context, id + "F19", {"entities" : qUnion([Q0, Q1, Q2, Q3, Q4, Q5, Q6, Q7, Q8, Q9, Q10, Q11, Q12, Q13, Q14, Q15]), "operationType" : NewBodyOperationType.REMOVE, "oppositeDirection" : true, "depth" : 5.08 * mm});
        }
    });
